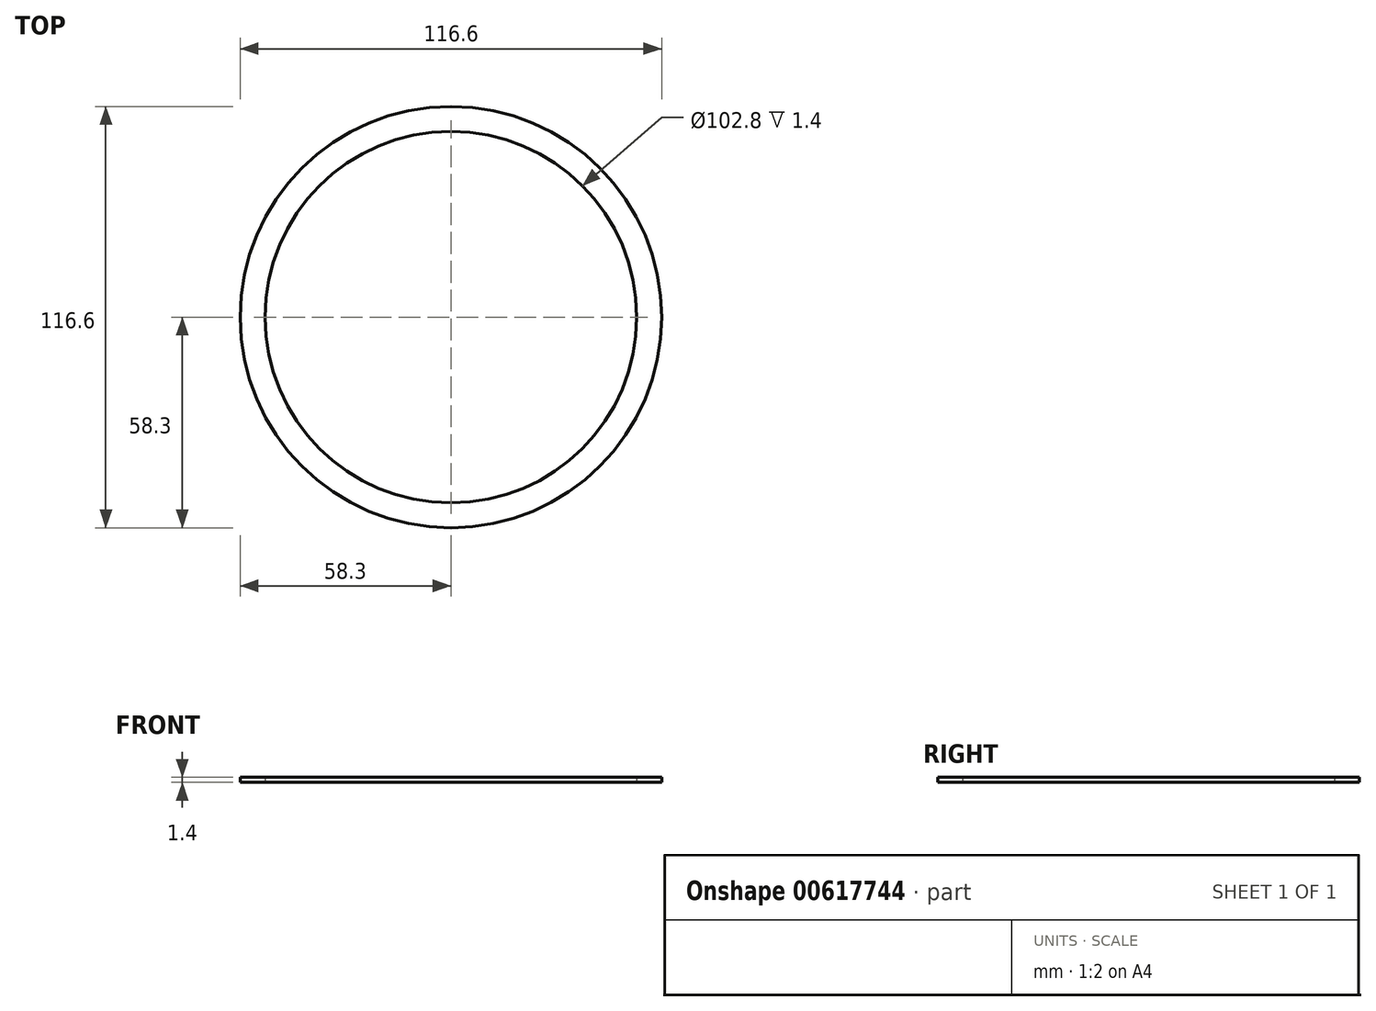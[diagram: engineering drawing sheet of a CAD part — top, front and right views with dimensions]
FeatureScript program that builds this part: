
annotation { "Feature Type Name" : "Feature", "Feature Type Description" : "" }
export const myFeature = defineFeature(function(context is Context, id is Id, definition is map)
    precondition{}
    {
        {
            var Q0;
            Q0=qCreatedBy(makeId("Top.planeOp"),FACE);
            var sketch = newSketch(context, id + "F0", { "sketchPlane" : qUnion([Q0])});
            skCircle(sketch, "E0", {"center": v(0, 0) * mm, "radius": 51.4 * mm});
            skCircle(sketch, "E1", {"center": v(0, 0) * mm, "radius": 58.3 * mm});
            skSolve(sketch);
        }
        {
            var Q0;
            Q0=makeQuery(id+"F0.imprint","IMPRINT",FACE,{"disambiguationData":[TD([[makeQuery(id+"F0.imprint","IMPRINT",EDGE,{"derivedFrom":sQuery(id+"F0.wireOp",EDGE,"E0")}),-1.0]])]});
            extrude(context, id + "F1", {"entities" : qUnion([Q0]), "depth" : 1.4 * mm, "offsetDistance" : 25 * mm});
        }
    });
